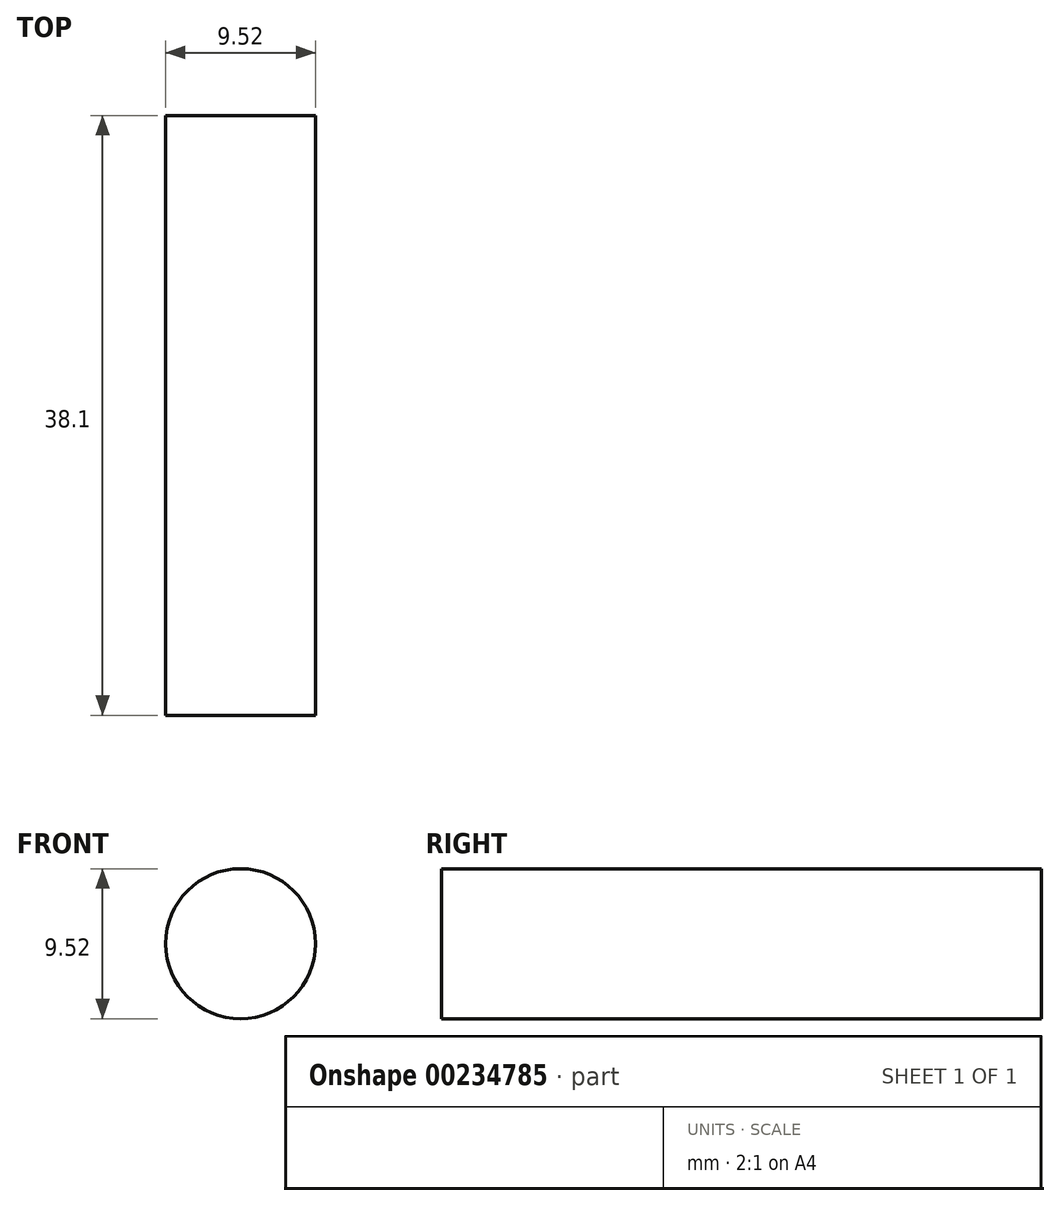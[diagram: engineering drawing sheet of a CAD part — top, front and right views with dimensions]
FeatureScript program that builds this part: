
annotation { "Feature Type Name" : "Feature", "Feature Type Description" : "" }
export const myFeature = defineFeature(function(context is Context, id is Id, definition is map)
    precondition{}
    {
        {
            var Q0;
            Q0=qCreatedBy(makeId("Front.planeOp"),FACE);
            var sketch = newSketch(context, id + "F1", { "sketchPlane" : qUnion([Q0])});
            skCircle(sketch, "E0", {"center": v(0, 0) * mm, "radius": 4.76 * mm});
            skSolve(sketch);
        }
        {
            var Q0;
            Q0=makeQuery(id+"F1.imprint","IMPRINT",FACE,{"disambiguationData":[TD([[makeQuery(id+"F1.imprint","IMPRINT",EDGE,{"derivedFrom":sQuery(id+"F1.wireOp",EDGE,"E0")}),1.0]])]});
            extrude(context, id + "F0", {"entities" : qUnion([Q0]), "depth" : 38.1 * mm});
        }
    });
